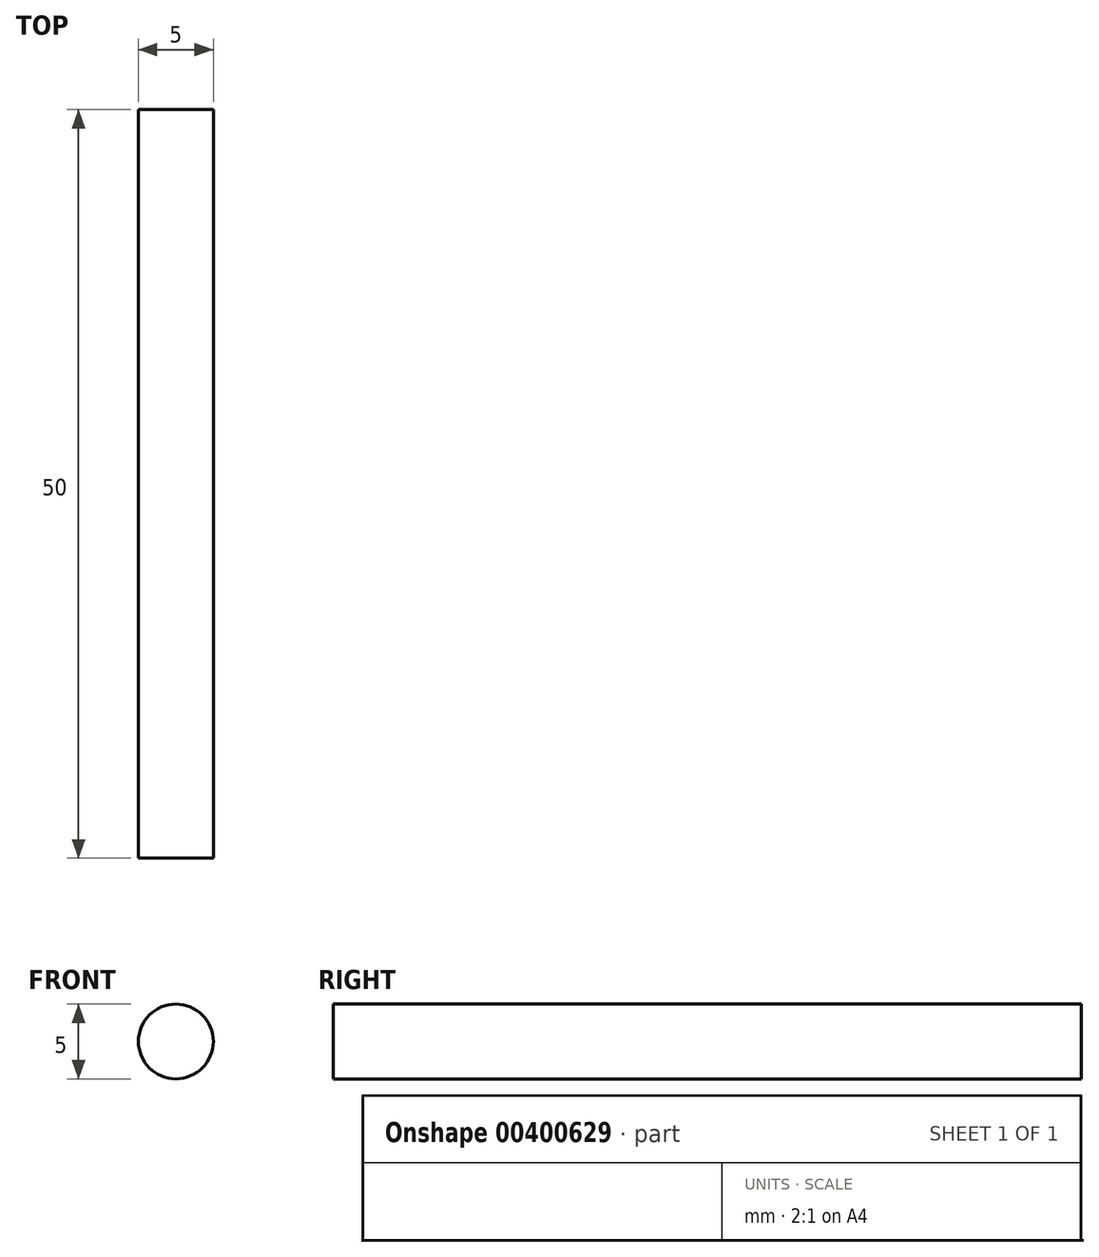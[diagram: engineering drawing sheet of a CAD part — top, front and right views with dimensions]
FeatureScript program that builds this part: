
annotation { "Feature Type Name" : "Feature", "Feature Type Description" : "" }
export const myFeature = defineFeature(function(context is Context, id is Id, definition is map)
    precondition{}
    {
        {
            var Q0;
            Q0=qCreatedBy(makeId("Front.planeOp"),FACE);
            var sketch = newSketch(context, id + "F0", { "sketchPlane" : qUnion([Q0])});
            skCircle(sketch, "E0", {"center": v(0, 0) * mm, "radius": 2.5 * mm});
            skSolve(sketch);
        }
        {
            var Q0;
            Q0 = qSketchRegion(id + "F0", true);
            extrude(context, id + "F1", {"entities" : qUnion([Q0]), "depth" : 50 * mm, "symmetric" : true});
        }
    });
